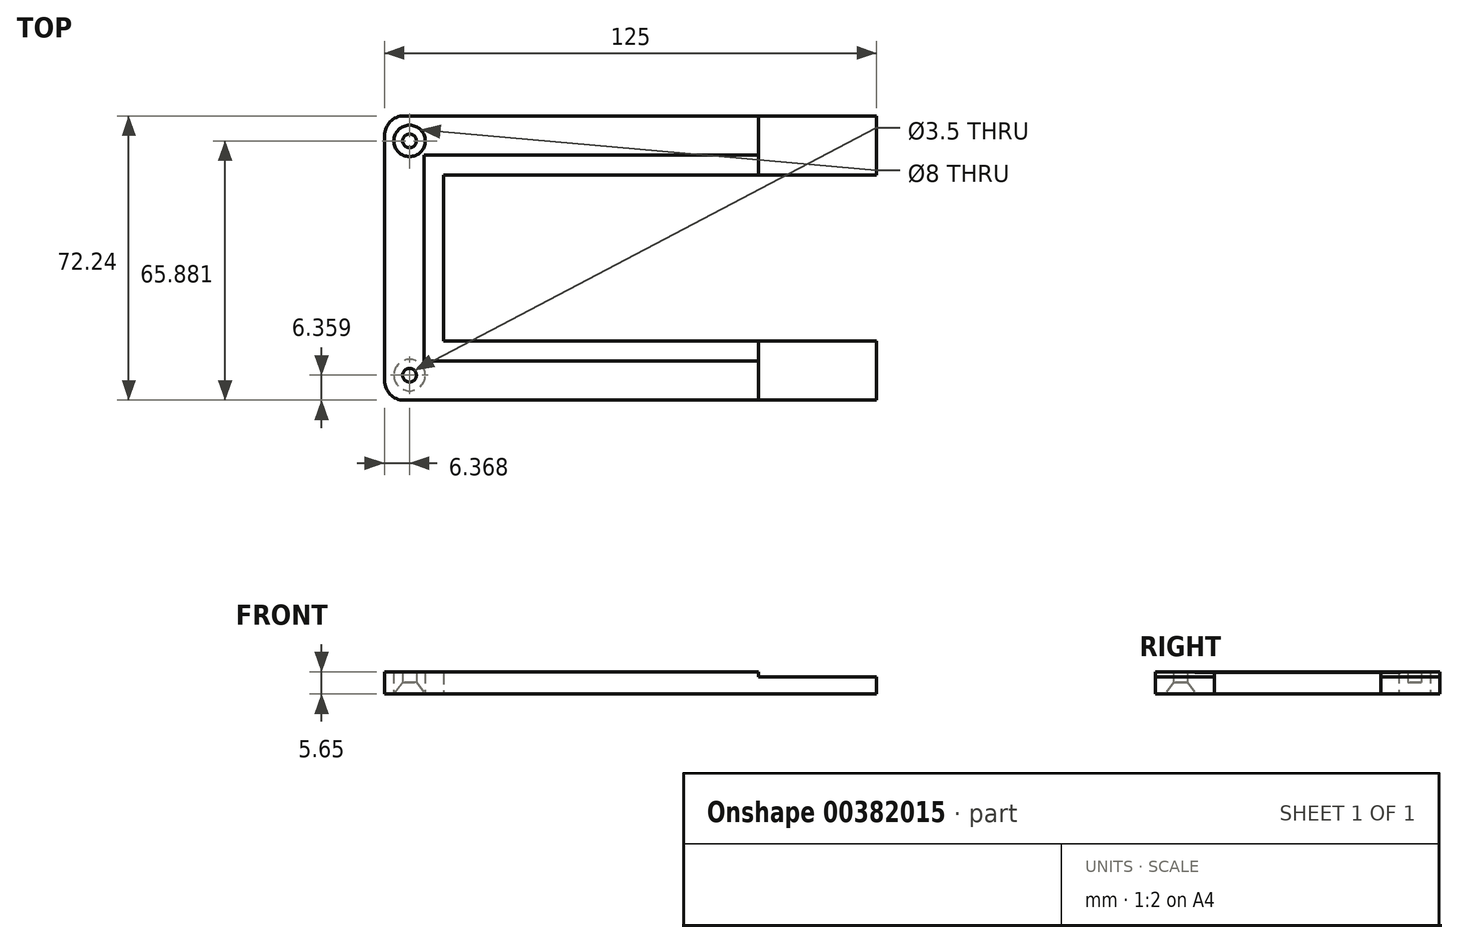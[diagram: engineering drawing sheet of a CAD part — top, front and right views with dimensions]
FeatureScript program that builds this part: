
annotation { "Feature Type Name" : "Feature", "Feature Type Description" : "" }
export const myFeature = defineFeature(function(context is Context, id is Id, definition is map)
    precondition{}
    {
        {
            var Q0;
            Q0=qCreatedBy(makeId("Top.planeOp"),FACE);
            var sketch = newSketch(context, id + "F0", { "sketchPlane" : qUnion([Q0])});
            skLineSegment(sketch, "E0.bottom", {"start": v(-143.35, 36.12) * mm, "end": v(86.65, 36.13) * mm});
            skLineSegment(sketch, "E0.top", {"start": v(-143.35, -36.13) * mm, "end": v(86.65, -36.12) * mm});
            skLineSegment(sketch, "E0.left", {"start": v(-143.35, 36.12) * mm, "end": v(-143.35, -36.13) * mm});
            skLineSegment(sketch, "E0.right", {"start": v(86.65, 36.13) * mm, "end": v(86.65, -36.12) * mm});
            skLineSegment(sketch, "E1.bottom", {"start": v(-128.35, 21.12) * mm, "end": v(71.65, 21.13) * mm});
            skLineSegment(sketch, "E1.top", {"start": v(-128.35, -21.13) * mm, "end": v(71.65, -21.12) * mm});
            skLineSegment(sketch, "E1.left", {"start": v(-128.35, 21.12) * mm, "end": v(-128.35, -21.13) * mm});
            skLineSegment(sketch, "E1.right", {"start": v(71.65, 21.13) * mm, "end": v(71.65, -21.12) * mm});
            skLineSegment(sketch, "E2.bottom", {"start": v(-133.35, 26.12) * mm, "end": v(76.65, 26.13) * mm});
            skLineSegment(sketch, "E2.top", {"start": v(-133.35, -26.13) * mm, "end": v(76.65, -26.12) * mm});
            skLineSegment(sketch, "E2.left", {"start": v(-133.35, 26.12) * mm, "end": v(-133.35, -26.13) * mm});
            skLineSegment(sketch, "E2.right", {"start": v(76.65, 26.13) * mm, "end": v(76.65, -26.12) * mm});
            skSolve(sketch);
        }
        {
            var Q0;
            Q0=makeQuery(id+"F0.imprint","IMPRINT",FACE,{"disambiguationData":[TD([[makeQuery(id+"F0.imprint","IMPRINT",EDGE,{"derivedFrom":sQuery(id+"F0.wireOp",EDGE,"E1.bottom")}),1.0]])]});
            extrude(context, id + "F1", {"entities" : qUnion([Q0]), "depth" : 5.5 * mm});
        }
        {
            var Q0;
            Q0=makeQuery(id+"F0.imprint","IMPRINT",FACE,{"disambiguationData":[TD([[makeQuery(id+"F0.imprint","IMPRINT",EDGE,{"derivedFrom":sQuery(id+"F0.wireOp",EDGE,"E0.bottom")}),-1.0]])]});
            extrude(context, id + "F2", {"entities" : qUnion([Q0]), "operationType" : NewBodyOperationType.ADD, "depth" : 5.65 * mm});
        }
        {
            var Q0;
            Q0=makeQuery(id+"F2.opExtrude","SWEPT_FACE",FACE,{"disambiguationData":[OSD([sQuery(id+"F0.wireOp",EDGE,"E0.top")])]});
            var sketch = newSketch(context, id + "F3", { "sketchPlane" : qUnion([Q0])});
            skPoint(sketch, "E3.orphan", {"position": v(66.65, 1.3) * mm});
            skPoint(sketch, "E4.start.orphan", {"position": v(-133.35, 1.3) * mm});
            skLineSegment(sketch, "E5", {"start": v(-48.35, 4.35) * mm, "end": v(-48.35, 5.65) * mm});
            skLineSegment(sketch, "E6", {"start": v(-18.35, 4.35) * mm, "end": v(-18.35, 0) * mm});
            skPoint(sketch, "E7.start.orphan", {"position": v(-13.35, 1.3) * mm});
            skPoint(sketch, "E8.end.orphan", {"position": v(-28.35, 5.65) * mm});
            skPoint(sketch, "E9.start.orphan", {"position": v(-33.35, 1.3) * mm});
            skLineSegment(sketch, "E10", {"start": v(-48.35, 4.35) * mm, "end": v(-18.35, 4.35) * mm});
            skSolve(sketch);
        }
        {
            var Q0;
            {var subQ3=sQuery(id+"F3.wireOp",EDGE,"E5");Q0=makeQuery(id+"F3.imprint","IMPRINT",FACE,{"disambiguationData":[TD([[makeQuery(id+"F3.imprint","IMPRINT",EDGE,{"derivedFrom":subQ3}),-1.0]])]});}
            extrude(context, id + "F4", {"entities" : qUnion([Q0]), "operationType" : NewBodyOperationType.REMOVE, "oppositeDirection" : true, "depth" : 100 * mm});
        }
        {
            var Q0;
            Q0=makeQuery(id+"F2.opExtrude","SWEPT_EDGE",EDGE,{"disambiguationData":[OSD([sQuery(id+"F0.wireOp",EDGE,"E0.bottom"),sQuery(id+"F0.wireOp",EDGE,"E0.left")])]});
            var Q1;
            Q1=makeQuery(id+"F2.opExtrude","SWEPT_EDGE",EDGE,{"disambiguationData":[OSD([sQuery(id+"F0.wireOp",EDGE,"E0.top"),sQuery(id+"F0.wireOp",EDGE,"E0.left")])]});
            fillet(context, id + "F5", {"entities" : qUnion([Q0, Q1]), "radius" : 5 * mm, "tangentPropagation" : true, "allowEdgeOverflow" : false});
        }
        {
            var Q0;
            Q0=makeQuery(id+"F0.imprint","IMPRINT",FACE,{"disambiguationData":[TD([[makeQuery(id+"F0.imprint","IMPRINT",EDGE,{"derivedFrom":sQuery(id+"F0.wireOp",EDGE,"E0.bottom")}),-1.0]])]});
            var sketch = newSketch(context, id + "F6", { "sketchPlane" : qUnion([Q0])});
            skCircle(sketch, "E11", {"center": v(-136.98, -29.76) * mm, "radius": 1.75 * mm});
            skCircle(sketch, "E12.MirrorC", {"center": v(-136.98, 29.76) * mm, "radius": 1.75 * mm});
            skCircle(sketch, "E13", {"center": v(-136.98, -29.76) * mm, "radius": 4 * mm});
            skCircle(sketch, "E14", {"center": v(-136.98, 29.76) * mm, "radius": 4 * mm});
            skSolve(sketch);
        }
        {
            var Q0;
            Q0=makeQuery(id+"F6.imprint","IMPRINT",FACE,{"disambiguationData":[TD([[makeQuery(id+"F6.imprint","IMPRINT",EDGE,{"derivedFrom":sQuery(id+"F6.wireOp",EDGE,"E12.MirrorC")}),-1.0]])]});
            var Q1;
            Q1=makeQuery(id+"F6.imprint","IMPRINT",FACE,{"disambiguationData":[TD([[makeQuery(id+"F6.imprint","IMPRINT",EDGE,{"derivedFrom":sQuery(id+"F6.wireOp",EDGE,"E11")}),1.0]])]});
            extrude(context, id + "F7", {"entities" : qUnion([Q0, Q1]), "operationType" : NewBodyOperationType.REMOVE, "depth" : 25 * mm});
        }
        {
            var Q0;
            Q0=makeQuery(id+"F6.imprint","IMPRINT",FACE,{"disambiguationData":[TD([[makeQuery(id+"F6.imprint","IMPRINT",EDGE,{"derivedFrom":sQuery(id+"F6.wireOp",EDGE,"E11")}),-1.0]])]});
            var Q1;
            Q1=makeQuery(id+"F6.imprint","IMPRINT",FACE,{"disambiguationData":[TD([[makeQuery(id+"F6.imprint","IMPRINT",EDGE,{"derivedFrom":sQuery(id+"F6.wireOp",EDGE,"E12.MirrorC")}),1.0]])]});
            extrude(context, id + "F8", {"entities" : qUnion([Q0, Q1]), "operationType" : NewBodyOperationType.REMOVE, "depth" : 3 * mm});
        }
        {
            var Q0;
            Q0=makeQuery(id+"F8.boolean.opBoolean","COPY",EDGE,{"derivedFrom":makeQuery(id+"F8.opExtrude","CAP_EDGE",EDGE,{"disambiguationData":[OSD([sQuery(id+"F6.wireOp",EDGE,"E14")])],"isStart":false})});
            var Q1;
            Q1=makeQuery(id+"F8.boolean.opBoolean","COPY",EDGE,{"derivedFrom":makeQuery(id+"F8.opExtrude","CAP_EDGE",EDGE,{"disambiguationData":[OSD([sQuery(id+"F6.wireOp",EDGE,"E13")])],"isStart":false})});
            chamfer(context, id + "F9", {"entities" : qUnion([Q0, Q1]), "chamferType" : ChamferType.OFFSET_ANGLE, "width" : 3 * mm, "oppositeDirection" : false, "angle" : 37 * degree, "tangentPropagation" : true});
        }
    });
